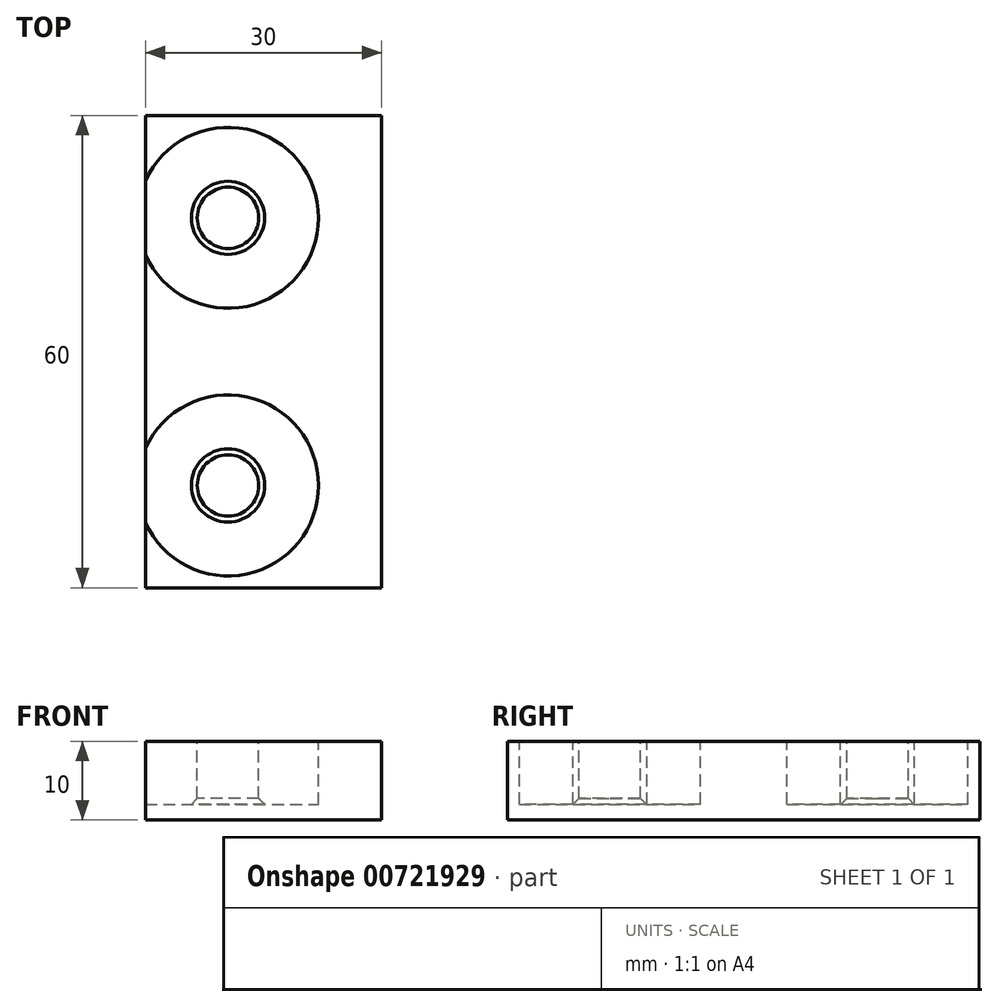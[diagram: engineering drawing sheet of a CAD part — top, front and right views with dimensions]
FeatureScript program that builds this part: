
annotation { "Feature Type Name" : "Feature", "Feature Type Description" : "" }
export const myFeature = defineFeature(function(context is Context, id is Id, definition is map)
    precondition{}
    {
        {
            var Q0;
            Q0=qCreatedBy(makeId("Top.planeOp"),FACE);
            var sketch = newSketch(context, id + "F0", { "sketchPlane" : qUnion([Q0])});
            skLineSegment(sketch, "E0.bottom", {"start": v(-15, -30) * mm, "end": v(15, -30) * mm});
            skLineSegment(sketch, "E0.top", {"start": v(-15, 30) * mm, "end": v(15, 30) * mm});
            skLineSegment(sketch, "E0.left", {"start": v(-15, -30) * mm, "end": v(-15, 30) * mm});
            skLineSegment(sketch, "E0.right", {"start": v(15, -30) * mm, "end": v(15, 30) * mm});
            skPoint(sketch, "E0.middle", {"position": v(0, 0) * mm});
            skCircle(sketch, "E1", {"center": v(-5, 17) * mm, "radius": 11 * mm, "construction": true});
            skLineSegment(sketch, "E2", {"start": v(15, 0) * mm, "end": v(-15, 0) * mm, "construction": true});
            skCircle(sketch, "E3.MirrorC", {"center": v(-5, -17) * mm, "radius": 11 * mm, "construction": true});
            skSolve(sketch);
        }
        {
            var Q0;
            Q0=makeQuery(id+"F0.imprint","IMPRINT",FACE,{"disambiguationData":[TD([[makeQuery(id+"F0.imprint","IMPRINT",EDGE,{"derivedFrom":sQuery(id+"F0.wireOp",EDGE,"E0.bottom")}),1.0]])]});
            extrude(context, id + "F1", {"entities" : qUnion([Q0]), "depth" : 10 * mm, "offsetDistance" : 25 * mm});
        }
        {
            var Q0;
            Q0=makeQuery(id+"F1.opExtrude","CAP_FACE",FACE,{"disambiguationData":[OSD([sQuery(id+"F0.wireOp",EDGE,"E0.bottom"),sQuery(id+"F0.wireOp",EDGE,"E0.top"),sQuery(id+"F0.wireOp",EDGE,"E0.left"),sQuery(id+"F0.wireOp",EDGE,"E0.right")])],"isStart":false});
            var sketch = newSketch(context, id + "F2", { "sketchPlane" : qUnion([Q0])});
            skLineSegment(sketch, "E4.bottom", {"start": v(-15, -30) * mm, "end": v(15, -30) * mm, "construction": true});
            skLineSegment(sketch, "E4.top", {"start": v(-15, 30) * mm, "end": v(15, 30) * mm, "construction": true});
            skLineSegment(sketch, "E4.left", {"start": v(-15, -30) * mm, "end": v(-15, 30) * mm, "construction": true});
            skLineSegment(sketch, "E4.right", {"start": v(15, -30) * mm, "end": v(15, 30) * mm, "construction": true});
            skPoint(sketch, "E4.middle", {"position": v(0, 0) * mm});
            skCircle(sketch, "E5", {"center": v(-4.5, 17) * mm, "radius": 11.5 * mm});
            skLineSegment(sketch, "E6", {"start": v(15, 0) * mm, "end": v(-15, 0) * mm, "construction": true});
            skCircle(sketch, "E7.MirrorC", {"center": v(-4.5, -17) * mm, "radius": 11.5 * mm});
            skCircle(sketch, "E8", {"center": v(-4.5, 17) * mm, "radius": 3.9 * mm});
            skCircle(sketch, "E9", {"center": v(-4.5, -17) * mm, "radius": 3.9 * mm});
            skSolve(sketch);
        }
        {
            var Q0;
            Q0=makeQuery(id+"F2.imprint","IMPRINT",FACE,{"disambiguationData":[TD([[makeQuery(id+"F2.imprint","IMPRINT",EDGE,{"derivedFrom":sQuery(id+"F2.wireOp",EDGE,"E8")}),-1.0]])]});
            var Q1;
            Q1=makeQuery(id+"F2.imprint","IMPRINT",FACE,{"disambiguationData":[TD([[makeQuery(id+"F2.imprint","IMPRINT",EDGE,{"derivedFrom":sQuery(id+"F2.wireOp",EDGE,"E9")}),-1.0]])]});
            extrude(context, id + "F3", {"entities" : qUnion([Q0, Q1]), "operationType" : NewBodyOperationType.REMOVE, "oppositeDirection" : true, "depth" : 8 * mm, "offsetDistance" : 25 * mm});
        }
        {
            var Q0;
            Q0=makeQuery(id+"F3.boolean.opBoolean","COPY",EDGE,{"derivedFrom":makeQuery(id+"F3.opExtrude","CAP_EDGE",EDGE,{"disambiguationData":[OSD([sQuery(id+"F2.wireOp",EDGE,"E8")])],"isStart":false})});
            var Q1;
            Q1=makeQuery(id+"F3.boolean.opBoolean","COPY",EDGE,{"derivedFrom":makeQuery(id+"F3.opExtrude","CAP_EDGE",EDGE,{"disambiguationData":[OSD([sQuery(id+"F2.wireOp",EDGE,"E9")])],"isStart":false})});
            chamfer(context, id + "F4", {"entities" : qUnion([Q0, Q1]), "width" : 0.75 * mm, "tangentPropagation" : true});
        }
    });
